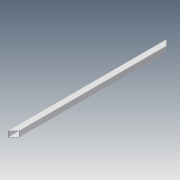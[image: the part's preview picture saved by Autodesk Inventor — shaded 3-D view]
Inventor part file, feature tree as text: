
AUTODESK INVENTOR PART (.ipt)
format: ipt  version: 2014 (Build 180170000, 170)  size: 112,128 bytes
history: native  units: in
note: dims shown in document units (in); Inventor stores cm internally (conversion verified against a paired STEP export)
features: extrude x2, sketch x2
ambient origin geometry x8: Origin, YZ Plane, XZ Plane, XY Plane, X Axis, Y Axis, Z Axis, Center Point
bodies: Solid1 (feature_tree)
feature tree (4):
  extrude  "Extrusion1"  Depth=1.0in
  extrude  "Extrusion2"  Depth=0.063in
  sketch  "Sketch1"  dims[d0=1.0in d1=1.0in]
  sketch  "Sketch2"  dims[d2=0.07in d3=0.063in d4=27.0in d5=0.0in d7=45.0deg d9=45.0deg d10=1.0in d11=0.0in]
